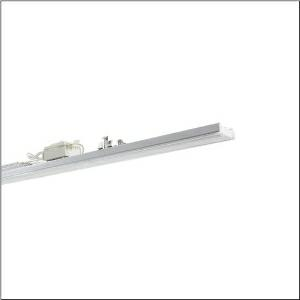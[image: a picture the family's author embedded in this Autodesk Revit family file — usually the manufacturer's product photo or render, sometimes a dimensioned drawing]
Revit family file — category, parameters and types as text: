
# Revit family: licross_r__21_recessed_mo_52te12dn4axg_78cf
name_source: partatom
category: Lighting Fixtures
units: mm (PartAtom-declared; Revit-internal decimal feet)

## family parameters
Cut with Voids When Loaded = No
Host = Face
Light Source = No
Part Type = Normal
Room Calculation Point = No
Round Connector Dimension = Use Diameter
Shared = No

## types (1)
- --- (1 x LED, 10280 lm, 58 W, 4000K)
    Apparent Load = 58 VA
    CIE Flux Codes = 72 92 99 100 100
    Color Rendering = 80
    Color Temperature = 4000K
    Default Elevation = 1800 mm
    Description = Licross® 21 Recessed MO, luminaire insert, of sheet steel, galvanised, coil coated, white, length: 1.500mm, width: 66mm, height: 67mm, LED rated luminous flux: 10.280lm, light colour: 840, control gear: DALI 2, with plug, 5-pole, with phase selection, mains connection: 220..240V, AC, 50/60Hz, rated input power: 58W, internal wiring halogen-free, primary optical cover: cover, of PMMA, light emission: direct distribution, primary light characteristic: symmetric, protection rating (complete): IP54, insulation class (complete): insulation class I (protective earthing), certification: CE, ENEC, VDE, UKCA, protection symbol: D if used in an environment with non-conductive dust loads with corresponding accessories, impact resistance: IK06, permissible ambient temperature for indoor applications: -25..+35°C, corresponds to IFS (International Featured Standards) requirements for safety and quality in the food industry, reducing of maximum allowable ambient temperature of 5°C with ceiling mounting, LABS conformity tested according to VDMA 24364:2018-05, packaging unit: 1 piece
    Height = 58 mm
    Lamp = 1 x LED
    Lamp Light Flux = 10280 lm
    Lamp Power = 58 W
    Lamp count = 1
    Length = 1500 mm
    Luminous efficacy = 177 lm/W
    Manufacturer = Siteco
    ModVariant = No
    Model = 52TE12DN4AXG
    Mounting Place = Ceiling
    Mounting Type = Pendant
    Number of Poles = 1
    OnlyDefault = Yes
    Power Factor = 1
    Product Name = Licross® 21 Recessed MO
    Product group = luminaire insert | ceiling pendant
    ProductGroupID = 902
    Protection Class = Protection class I
    Protection Degree = IP 54
    RLX_Detail_Level = 1
    RLX_Emergency_Light_Flux = 0 lm
    RLX_Emergency_Type = 0
    RLX_Emergency_Type_DB = No
    RlxData = <blob elided: 24681 chars, md5=752e9d7b>
    Socket = socket
    Standby Power = 0 W
    System Light Flux = 10280 lm
    System Power = 58 W
    Type Comments = factory setting: luminous flux: 100 % | dim-lin: 254 | 390 mA
    Type Image = l_1296930.jpg
    URL = http://relux.com
    VarID = @adj_147653
    Voltage = 0 V
    Weight = 0.00 kg
    Width = 66 mm

## geometry (parser evidence)
native form markers: Blend x4, Sweep x12
no freeform markers — native parametric forms only
